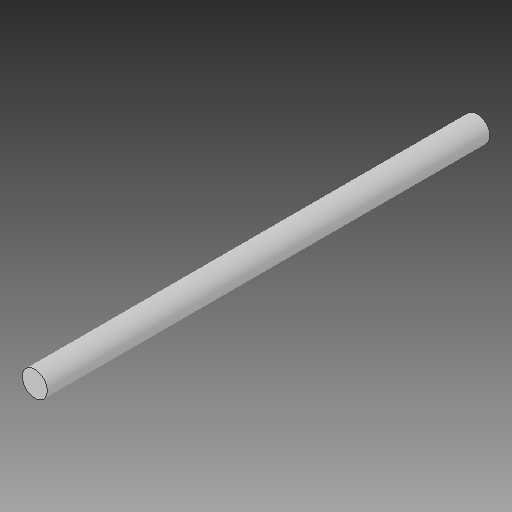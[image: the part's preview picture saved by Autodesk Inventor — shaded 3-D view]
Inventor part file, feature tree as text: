
AUTODESK INVENTOR PART (.ipt)
format: ipt  version: 2019 (Build 230136000, 136)  size: 76,800 bytes
history: native  units: in
note: dims shown in document units (in); Inventor stores cm internally (conversion verified against a paired STEP export)
features: other x3, sketch x1
ambient origin geometry x8: Origin, YZ Plane, XZ Plane, XY Plane, X Axis, Y Axis, Z Axis, Center Point
bodies: Solid1 (feature_tree)
feature tree (4):
  other  "4inax.ipt"
  other  "Solid1::4inax.ipt"
  other  "TaggingFeature1"
  sketch  "Sketch1"  dims[d0=0.3937in]
